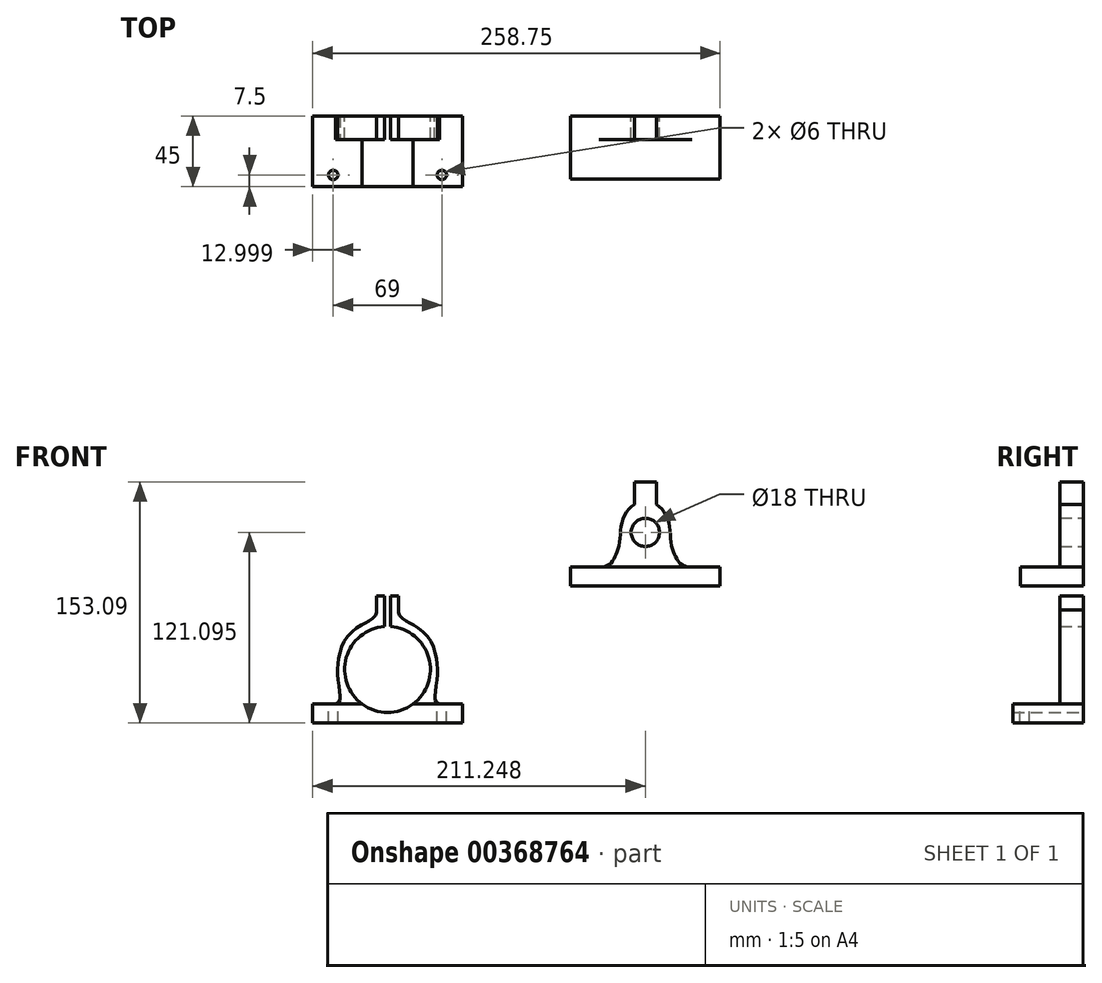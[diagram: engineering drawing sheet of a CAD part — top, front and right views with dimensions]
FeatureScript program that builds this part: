
annotation { "Feature Type Name" : "Feature", "Feature Type Description" : "" }
export const myFeature = defineFeature(function(context is Context, id is Id, definition is map)
    precondition{}
    {
        {
            var Q0;
            Q0=qCreatedBy(makeId("Front.planeOp"),FACE);
            var sketch = newSketch(context, id + "F0", { "sketchPlane" : qUnion([Q0])});
            skLineSegment(sketch, "E0", {"start": v(-93.8, 148.82) * mm, "end": v(-100.8, 148.82) * mm});
            skLineSegment(sketch, "E1", {"start": v(-100.8, 148.82) * mm, "end": v(-100.8, 134.43) * mm});
            skFitSpline(sketch, "E2", {"points": [v(-100.8, 134.43) * mm, v(-106.63, 128.23) * mm, v(-109.38, 119.14) * mm, v(-110.23, 109.7) * mm, v(-112.07, 103.39) * mm, v(-113.8, 99.96) * mm, v(-117.07, 96.12) * mm, v(-123.3, 94.82) * mm], "startDerivative": vector(-41.03, -17.29) * mm, "endDerivative": vector(-26.14, 0) * mm});
            skLineSegment(sketch, "E3", {"start": v(-123.3, 94.82) * mm, "end": v(-141.3, 94.82) * mm});
            skLineSegment(sketch, "E4", {"start": v(-141.3, 94.82) * mm, "end": v(-141.3, 82.82) * mm});
            skLineSegment(sketch, "E5", {"start": v(-141.3, 82.82) * mm, "end": v(-93.8, 82.82) * mm});
            skLineSegment(sketch, "E6", {"start": v(-93.8, 82.82) * mm, "end": v(-93.8, 107.82) * mm});
            skArc(sketch, "E7", {"start": v(-93.8, 125.82) * mm, "mid": v(-102.8, 116.82) * mm, "end": v(-93.8, 107.82) * mm});
            skLineSegment(sketch, "E8", {"start": v(-93.8, 125.82) * mm, "end": v(-93.8, 148.82) * mm});
            skPoint(sketch, "E9", {"position": v(-128.3, 94.82) * mm});
            skLineSegment(sketch, "E10.MirrorCS", {"start": v(-93.8, 148.82) * mm, "end": v(-86.8, 148.82) * mm});
            skLineSegment(sketch, "E11.MirrorCS", {"start": v(-46.3, 82.82) * mm, "end": v(-93.8, 82.82) * mm});
            skLineSegment(sketch, "E12.MirrorCS", {"start": v(-46.3, 94.82) * mm, "end": v(-46.3, 82.82) * mm});
            skLineSegment(sketch, "E13.MirrorCS", {"start": v(-64.3, 94.82) * mm, "end": v(-46.3, 94.82) * mm});
            skFitSpline(sketch, "E14.MirrorCS", {"points": [v(-86.8, 134.43) * mm, v(-80.95, 128.23) * mm, v(-78.2, 119.14) * mm, v(-77.35, 109.7) * mm, v(-75.52, 103.39) * mm, v(-73.79, 99.96) * mm, v(-70.5, 96.12) * mm, v(-64.3, 94.82) * mm], "startDerivative": vector(41.03, -17.29) * mm, "endDerivative": vector(26.14, 0) * mm});
            skLineSegment(sketch, "E15.MirrorCS", {"start": v(-86.8, 148.82) * mm, "end": v(-86.8, 134.43) * mm});
            skArc(sketch, "E16.MirrorCS", {"start": v(-93.8, 125.82) * mm, "mid": v(-84.8, 116.82) * mm, "end": v(-93.8, 107.82) * mm});
            skPoint(sketch, "E17.MirrorP", {"position": v(-59.3, 94.82) * mm});
            skCircle(sketch, "E18", {"center": v(-257.54, 29.73) * mm, "radius": 27.25 * mm});
            skFitSpline(sketch, "E19", {"points": [v(-290.46, 7.73) * mm, v(-287.85, 9.94) * mm, v(-287.98, 16.09) * mm, v(-289.33, 27.52) * mm, v(-288.47, 37.36) * mm, v(-283.92, 49.4) * mm, v(-274.33, 57.89) * mm, v(-268.3, 61.2) * mm, v(-264.74, 65.02) * mm, v(-264.54, 67.48) * mm], "startDerivative": vector(50.74, 19) * mm, "endDerivative": vector(1.63, 36.85) * mm});
            skLineSegment(sketch, "E20", {"start": v(-264.54, 67.48) * mm, "end": v(-264.54, 76.3) * mm});
            skLineSegment(sketch, "E21", {"start": v(-264.54, 76.3) * mm, "end": v(-259.54, 76.3) * mm});
            skLineSegment(sketch, "E22", {"start": v(-259.54, 76.3) * mm, "end": v(-259.54, 56.9) * mm});
            skLineSegment(sketch, "E23", {"start": v(-290.46, 7.73) * mm, "end": v(-305.04, 7.73) * mm});
            skLineSegment(sketch, "E24", {"start": v(-305.04, 7.73) * mm, "end": v(-305.04, -4.27) * mm});
            skLineSegment(sketch, "E25", {"start": v(-305.04, -4.27) * mm, "end": v(-257.6, -4.27) * mm});
            skLineSegment(sketch, "E26", {"start": v(-257.6, -4.27) * mm, "end": v(-257.6, 2.48) * mm});
            skLineSegment(sketch, "E27.MirrorCS", {"start": v(-250.54, 67.48) * mm, "end": v(-250.54, 76.3) * mm});
            skLineSegment(sketch, "E28.MirrorCS", {"start": v(-250.54, 76.3) * mm, "end": v(-255.54, 76.3) * mm});
            skLineSegment(sketch, "E29.MirrorCS", {"start": v(-255.54, 76.3) * mm, "end": v(-255.54, 56.9) * mm});
            skLineSegment(sketch, "E30.MirrorCS", {"start": v(-210.04, -4.27) * mm, "end": v(-257.48, -4.27) * mm});
            skLineSegment(sketch, "E31.MirrorCS", {"start": v(-210.04, 7.73) * mm, "end": v(-210.04, -4.27) * mm});
            skFitSpline(sketch, "E32.MirrorCS", {"points": [v(-224.63, 7.73) * mm, v(-227.23, 9.94) * mm, v(-227.1, 16.09) * mm, v(-225.75, 27.52) * mm, v(-226.61, 37.36) * mm, v(-231.16, 49.4) * mm, v(-240.75, 57.89) * mm, v(-246.78, 61.2) * mm, v(-250.34, 65.02) * mm, v(-250.54, 67.48) * mm], "startDerivative": vector(-50.74, 19) * mm, "endDerivative": vector(-1.63, 36.85) * mm});
            skLineSegment(sketch, "E33.MirrorCS", {"start": v(-224.63, 7.73) * mm, "end": v(-210.04, 7.73) * mm});
            skLineSegment(sketch, "E34", {"start": v(-305.04, -4.27) * mm, "end": v(-210.04, -4.27) * mm});
            skSolve(sketch);
        }
        {
            var Q0;
            Q0=makeQuery(id+"F0.imprint","IMPRINT",FACE,{"disambiguationData":[TD([[makeQuery(id+"F0.imprint","IMPRINT",EDGE,{"derivedFrom":sQuery(id+"F0.wireOp",EDGE,"E6")}),-1.0]])]});
            var Q1;
            Q1=makeQuery(id+"F0.imprint","IMPRINT",FACE,{"disambiguationData":[TD([[makeQuery(id+"F0.imprint","IMPRINT",EDGE,{"derivedFrom":sQuery(id+"F0.wireOp",EDGE,"E0")}),1.0]])]});
            var Q2;
            Q2=makeQuery(id+"F0.imprint","IMPRINT",FACE,{"disambiguationData":[TD([[makeQuery(id+"F0.imprint","IMPRINT",EDGE,{"derivedFrom":sQuery(id+"F0.wireOp",EDGE,"E19")}),-1.0]])]});
            var Q3;
            {var subQ1=sQuery(id+"F0.wireOp",EDGE,"E26");Q3=makeQuery(id+"F0.imprint","IMPRINT",FACE,{"disambiguationData":[TD([[makeQuery(id+"F0.imprint","IMPRINT",EDGE,{"derivedFrom":subQ1}),-1.0]])]});}
            extrude(context, id + "F1", {"entities" : qUnion([Q0, Q1, Q2, Q3]), "depth" : 15 * mm, "offsetDistance" : 25 * mm});
        }
        {
            var Q0;
            Q0=makeQuery(id+"F1.opExtrude","CAP_FACE",FACE,{"disambiguationData":[OSD([sQuery(id+"F0.wireOp",EDGE,"E0"),sQuery(id+"F0.wireOp",EDGE,"E1"),sQuery(id+"F0.wireOp",EDGE,"E2"),sQuery(id+"F0.wireOp",EDGE,"E3"),sQuery(id+"F0.wireOp",EDGE,"E4"),sQuery(id+"F0.wireOp",EDGE,"E5"),sQuery(id+"F0.wireOp",EDGE,"E7"),sQuery(id+"F0.wireOp",EDGE,"E10.MirrorCS"),sQuery(id+"F0.wireOp",EDGE,"E11.MirrorCS"),sQuery(id+"F0.wireOp",EDGE,"E12.MirrorCS"),sQuery(id+"F0.wireOp",EDGE,"E13.MirrorCS"),sQuery(id+"F0.wireOp",EDGE,"E14.MirrorCS"),sQuery(id+"F0.wireOp",EDGE,"E15.MirrorCS"),sQuery(id+"F0.wireOp",EDGE,"E16.MirrorCS")])],"isStart":false});
            var sketch = newSketch(context, id + "F2", { "sketchPlane" : qUnion([Q0])});
            skLineSegment(sketch, "E35.bottom", {"start": v(-141.3, 82.82) * mm, "end": v(-46.3, 82.82) * mm});
            skLineSegment(sketch, "E35.top", {"start": v(-141.3, 94.82) * mm, "end": v(-46.3, 94.82) * mm});
            skLineSegment(sketch, "E35.left", {"start": v(-141.3, 82.82) * mm, "end": v(-141.3, 94.82) * mm});
            skLineSegment(sketch, "E35.right", {"start": v(-46.3, 82.82) * mm, "end": v(-46.3, 94.82) * mm});
            skSolve(sketch);
        }
        {
            var Q0;
            Q0 = qSketchRegion(id + "F2", true);
            extrude(context, id + "F3", {"entities" : qUnion([Q0]), "operationType" : NewBodyOperationType.ADD, "depth" : 25 * mm, "offsetDistance" : 25 * mm});
        }
        {
            var Q0;
            Q0=makeQuery(id+"F1.opExtrude","CAP_FACE",FACE,{"disambiguationData":[OSD([sQuery(id+"F0.wireOp",EDGE,"E19"),sQuery(id+"F0.wireOp",EDGE,"E20"),sQuery(id+"F0.wireOp",EDGE,"E21"),sQuery(id+"F0.wireOp",EDGE,"E22"),sQuery(id+"F0.wireOp",EDGE,"E23"),sQuery(id+"F0.wireOp",EDGE,"E24"),sQuery(id+"F0.wireOp",EDGE,"E29.MirrorCS"),sQuery(id+"F0.wireOp",EDGE,"E27.MirrorCS"),sQuery(id+"F0.wireOp",EDGE,"E28.MirrorCS"),sQuery(id+"F0.wireOp",EDGE,"E31.MirrorCS"),sQuery(id+"F0.wireOp",EDGE,"E32.MirrorCS"),sQuery(id+"F0.wireOp",EDGE,"E18"),sQuery(id+"F0.wireOp",EDGE,"E33.MirrorCS"),sQuery(id+"F0.wireOp",EDGE,"E34")])],"isStart":false});
            var sketch = newSketch(context, id + "F4", { "sketchPlane" : qUnion([Q0])});
            skLineSegment(sketch, "E36.bottom", {"start": v(-305.04, -4.27) * mm, "end": v(-210.04, -4.27) * mm});
            skLineSegment(sketch, "E36.top", {"start": v(-305.04, 7.73) * mm, "end": v(-210.04, 7.73) * mm});
            skLineSegment(sketch, "E36.left", {"start": v(-305.04, -4.27) * mm, "end": v(-305.04, 7.73) * mm});
            skLineSegment(sketch, "E36.right", {"start": v(-210.04, -4.27) * mm, "end": v(-210.04, 7.73) * mm});
            skSolve(sketch);
        }
        {
            var Q0;
            Q0=makeQuery(id+"F4.imprint","IMPRINT",FACE,{"disambiguationData":[TD([[makeQuery(id+"F4.imprint","IMPRINT",EDGE,{"derivedFrom":sQuery(id+"F4.wireOp",EDGE,"E36.bottom")}),1.0]])]});
            extrude(context, id + "F5", {"entities" : qUnion([Q0]), "operationType" : NewBodyOperationType.ADD, "depth" : 30 * mm, "offsetDistance" : 25 * mm});
        }
        {
            var Q0;
            {var subQ0=sQuery(id+"F4.wireOp",EDGE,"E36.top");Q0=makeQuery(id+"F5.boolean.opBoolean","MERGE",FACE,{"derivedFrom":[makeQuery(id+"F1.opExtrude","SWEPT_FACE",FACE,{"disambiguationData":[OSD([sQuery(id+"F0.wireOp",EDGE,"E23")])]}),makeQuery(id+"F5.opExtrude","SWEPT_FACE",FACE,{"disambiguationData":[OSD([subQ0]),TDD([makeQuery(id+"F4.imprint","IMPRINT",EDGE,{"disambiguationData":[TD([[makeQuery(id+"F4.imprint","INTERSECT",VERTEX,{"disambiguationData":[OD(0.0)],"derivedFrom":[makeQuery(id+"F1.opExtrude","CAP_EDGE",EDGE,{"disambiguationData":[OSD([sQuery(id+"F0.wireOp",EDGE,"E18")])],"isStart":false}),subQ0]}),1.0]])],"derivedFrom":subQ0}),makeQuery(id+"F4.imprint","IMPRINT",EDGE,{"disambiguationData":[TD([[makeQuery(id+"F4.imprint","INTERSECT",VERTEX,{"derivedFrom":[subQ0,sQuery(id+"F4.wireOp",EDGE,"E36.left")]}),1.0]])],"derivedFrom":subQ0})])]})]});}
            var sketch = newSketch(context, id + "F6", { "sketchPlane" : qUnion([Q0])});
            skCircle(sketch, "E37", {"center": v(-292.04, -37.5) * mm, "radius": 3 * mm});
            skCircle(sketch, "E38", {"center": v(-223.04, -37.5) * mm, "radius": 3 * mm});
            skLineSegment(sketch, "E39.bottom", {"start": v(-305.04, -45) * mm, "end": v(-210.04, -45) * mm});
            skLineSegment(sketch, "E39.top", {"start": v(-305.04, -30) * mm, "end": v(-210.04, -30) * mm});
            skLineSegment(sketch, "E39.left", {"start": v(-305.04, -45) * mm, "end": v(-305.04, -30) * mm});
            skLineSegment(sketch, "E39.right", {"start": v(-210.04, -45) * mm, "end": v(-210.04, -30) * mm});
            skPoint(sketch, "E40", {"position": v(-305.04, -37.5) * mm});
            skSolve(sketch);
        }
        {
            var Q0;
            Q0=makeQuery(id+"F6.imprint","IMPRINT",FACE,{"disambiguationData":[TD([[makeQuery(id+"F6.imprint","IMPRINT",EDGE,{"derivedFrom":sQuery(id+"F6.wireOp",EDGE,"E37")}),1.0]])]});
            var Q1;
            Q1=makeQuery(id+"F6.imprint","IMPRINT",FACE,{"disambiguationData":[TD([[makeQuery(id+"F6.imprint","IMPRINT",EDGE,{"derivedFrom":sQuery(id+"F6.wireOp",EDGE,"E38")}),1.0]])]});
            extrude(context, id + "F7", {"entities" : qUnion([Q0, Q1]), "operationType" : NewBodyOperationType.REMOVE, "oppositeDirection" : true, "depth" : 25 * mm, "offsetDistance" : 25 * mm});
        }
    });
